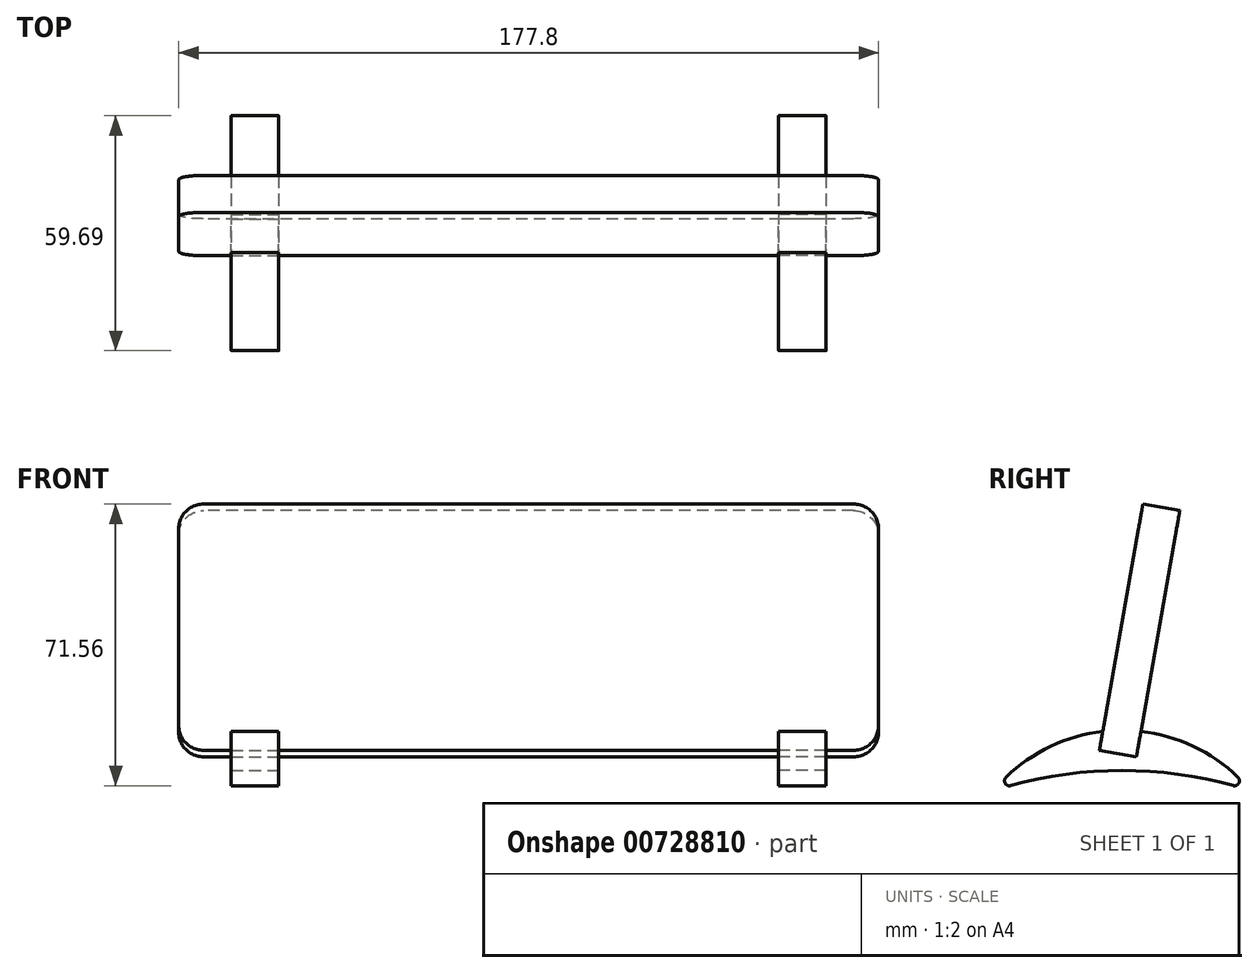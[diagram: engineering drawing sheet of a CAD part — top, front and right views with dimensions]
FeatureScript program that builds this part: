
annotation { "Feature Type Name" : "Feature", "Feature Type Description" : "" }
export const myFeature = defineFeature(function(context is Context, id is Id, definition is map)
    precondition{}
    {
        {
            var Q0;
            Q0=qCreatedBy(makeId("Right.planeOp"),FACE);
            var sketch = newSketch(context, id + "F0", { "sketchPlane" : qUnion([Q0])});
            skLineSegment(sketch, "E0.bottom", {"start": v(10.2, 30.44) * mm, "end": v(0.82, 32.1) * mm});
            skLineSegment(sketch, "E0.top", {"start": v(-0.82, -32.1) * mm, "end": v(-10.2, -30.44) * mm});
            skLineSegment(sketch, "E0.left", {"start": v(10.2, 30.44) * mm, "end": v(-0.82, -32.1) * mm});
            skLineSegment(sketch, "E0.right", {"start": v(0.82, 32.1) * mm, "end": v(-10.2, -30.44) * mm});
            skPoint(sketch, "E0.middle", {"position": v(0, 0) * mm});
            skSolve(sketch);
        }
        {
            var Q0;
            Q0=makeQuery(id+"F0.imprint","IMPRINT",FACE,{"disambiguationData":[TD([[makeQuery(id+"F0.imprint","IMPRINT",EDGE,{"derivedFrom":sQuery(id+"F0.wireOp",EDGE,"E0.bottom")}),1.0]])]});
            extrude(context, id + "F1", {"entities" : qUnion([Q0]), "endBound" : BoundingType.SYMMETRIC, "depth" : 177.8 * mm, "offsetDistance" : 25.4 * mm});
        }
        {
            var Q0;
            Q0=makeQuery(id+"F1.opExtrude","CAP_EDGE",EDGE,{"disambiguationData":[OSD([sQuery(id+"F0.wireOp",EDGE,"E0.bottom")])],"isStart":false});
            var Q1;
            Q1=makeQuery(id+"F1.opExtrude","CAP_EDGE",EDGE,{"disambiguationData":[OSD([sQuery(id+"F0.wireOp",EDGE,"E0.top")])],"isStart":false});
            var Q2;
            Q2=makeQuery(id+"F1.opExtrude","CAP_EDGE",EDGE,{"disambiguationData":[OSD([sQuery(id+"F0.wireOp",EDGE,"E0.bottom")])],"isStart":true});
            var Q3;
            Q3=makeQuery(id+"F1.opExtrude","CAP_EDGE",EDGE,{"disambiguationData":[OSD([sQuery(id+"F0.wireOp",EDGE,"E0.top")])],"isStart":true});
            fillet(context, id + "F2", {"entities" : qUnion([Q0, Q1, Q2, Q3]), "radius" : 6.35 * mm, "tangentPropagation" : true, "allowEdgeOverflow" : false});
        }
        {
            var Q0;
            Q0=qCreatedBy(makeId("Right.planeOp"),FACE);
            cPlane(context, id + "F3", {"entities" : qUnion([Q0]), "cplaneType" : CPlaneType.OFFSET, "offset" : 63.5 * mm, "width" : 152.4 * mm, "height" : 152.4 * mm});
        }
        {
            var Q0;
            Q0=qCreatedBy(id+"F3.planeOp",FACE);
            var sketch = newSketch(context, id + "F4", { "sketchPlane" : qUnion([Q0])});
            skLineSegment(sketch, "E1.0", {"start": v(-0.28, 25.84) * mm, "end": v(-9.1, -24.19) * mm, "construction": true});
            skLineSegment(sketch, "E2.0", {"start": v(-10.2, -30.44) * mm, "end": v(-9.1, -24.19) * mm, "construction": true});
            skLineSegment(sketch, "E3.0", {"start": v(-0.82, -32.1) * mm, "end": v(-10.2, -30.44) * mm, "construction": true});
            skLineSegment(sketch, "E4.0", {"start": v(0.28, -25.84) * mm, "end": v(-0.82, -32.1) * mm, "construction": true});
            skLineSegment(sketch, "E5.0", {"start": v(9.1, 24.19) * mm, "end": v(0.28, -25.84) * mm, "construction": true});
            skLineSegment(sketch, "E6", {"start": v(0, 0) * mm, "end": v(-19.23, -109.04) * mm, "construction": true});
            skArc(sketch, "E7", {"start": v(24.98, -37.28) * mm, "mid": v(-4.48, -25.4) * mm, "end": v(-33.94, -37.28) * mm, "construction": true});
            skLineSegment(sketch, "E8", {"start": v(-23.52, -25.4) * mm, "end": v(40.68, -25.4) * mm, "construction": true});
            skLineSegment(sketch, "E9", {"start": v(-4.48, -25.4) * mm, "end": v(-4.48, -61.74) * mm, "construction": true});
            skArc(sketch, "E10", {"start": v(23.76, -39.42) * mm, "mid": v(-4.48, -35.56) * mm, "end": v(-32.71, -39.42) * mm});
            skPoint(sketch, "E11.visualSharp", {"position": v(-37.17, -40.77) * mm});
            skArc(sketch, "E11.filletArc", {"start": v(-33.94, -37.28) * mm, "mid": v(-34.16, -38.83) * mm, "end": v(-32.71, -39.42) * mm});
            skPoint(sketch, "E12.visualSharp", {"position": v(28.21, -40.77) * mm});
            skArc(sketch, "E12.filletArc", {"start": v(23.76, -39.42) * mm, "mid": v(25.2, -38.83) * mm, "end": v(24.98, -37.28) * mm});
            skLineSegment(sketch, "E13", {"start": v(-10.2, -30.44) * mm, "end": v(-9.36, -25.68) * mm});
            skLineSegment(sketch, "E14", {"start": v(0.3, -25.67) * mm, "end": v(-0.82, -32.1) * mm});
            skLineSegment(sketch, "E15", {"start": v(-10.2, -30.44) * mm, "end": v(-0.82, -32.1) * mm});
            skArc(sketch, "E16", {"start": v(24.98, -37.28) * mm, "mid": v(13.6, -29.44) * mm, "end": v(0.3, -25.67) * mm});
            skArc(sketch, "E17.trimOffspring", {"start": v(-9.36, -25.68) * mm, "mid": v(-22.6, -29.46) * mm, "end": v(-33.94, -37.28) * mm});
            skLineSegment(sketch, "E18.trimOffspring", {"start": v(-4.48, -25.4) * mm, "end": v(-4.48, -25.4) * mm});
            skSolve(sketch);
        }
        {
            var Q0;
            Q0=makeQuery(id+"F4.imprint","IMPRINT",FACE,{"disambiguationData":[TD([[makeQuery(id+"F4.imprint","IMPRINT",EDGE,{"derivedFrom":sQuery(id+"F4.wireOp",EDGE,"E10")}),-1.0]])]});
            extrude(context, id + "F5", {"entities" : qUnion([Q0]), "depth" : 12.06 * mm, "offsetDistance" : 25.4 * mm});
        }
        {
            var Q0;
            Q0=makeQuery(id+"F5.opExtrude","SWEPT_BODY",BODY,{"disambiguationData":[OSD([sQuery(id+"F4.wireOp",EDGE,"E10"),sQuery(id+"F4.wireOp",EDGE,"E11.filletArc"),sQuery(id+"F4.wireOp",EDGE,"E12.filletArc"),sQuery(id+"F4.wireOp",EDGE,"E13"),sQuery(id+"F4.wireOp",EDGE,"E14"),sQuery(id+"F4.wireOp",EDGE,"E15"),sQuery(id+"F4.wireOp",EDGE,"E16"),sQuery(id+"F4.wireOp",EDGE,"E17.trimOffspring")])]});
            var Q1;
            Q1=qCreatedBy(makeId("Right.planeOp"),FACE);
            mirror(context, id + "F6", {"entities" : qUnion([Q0]), "mirrorPlane" : qUnion([Q1])});
        }
    });
